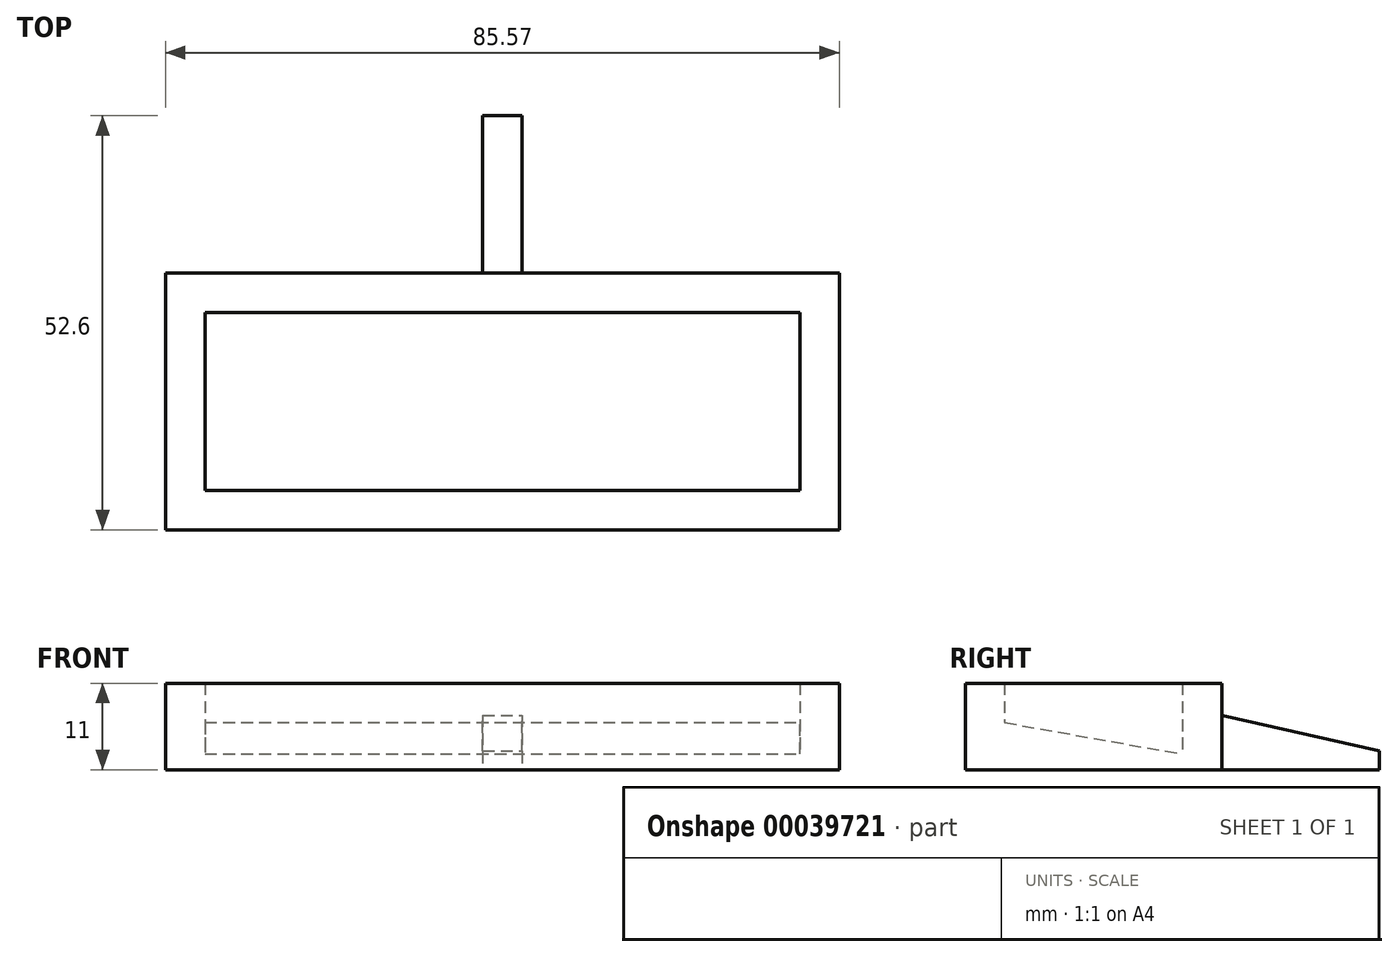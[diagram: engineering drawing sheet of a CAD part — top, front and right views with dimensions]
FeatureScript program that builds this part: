
annotation { "Feature Type Name" : "Feature", "Feature Type Description" : "" }
export const myFeature = defineFeature(function(context is Context, id is Id, definition is map)
    precondition{}
    {
        {
            var Q0;
            Q0=qCreatedBy(makeId("Top.planeOp"),FACE);
            var sketch = newSketch(context, id + "F0", { "sketchPlane" : qUnion([Q0])});
            skLineSegment(sketch, "E0.bottom", {"start": v(0, 0) * mm, "end": v(75.57, 0) * mm});
            skLineSegment(sketch, "E0.top", {"start": v(0, -22.6) * mm, "end": v(75.57, -22.6) * mm});
            skLineSegment(sketch, "E0.left", {"start": v(0, 0) * mm, "end": v(0, -22.6) * mm});
            skLineSegment(sketch, "E0.right", {"start": v(75.57, 0) * mm, "end": v(75.57, -22.6) * mm});
            skLineSegment(sketch, "E1.bottom", {"start": v(-5, 5) * mm, "end": v(80.57, 5) * mm});
            skLineSegment(sketch, "E1.top", {"start": v(-5, -27.6) * mm, "end": v(80.57, -27.6) * mm});
            skLineSegment(sketch, "E1.left", {"start": v(-5, 5) * mm, "end": v(-5, -27.6) * mm});
            skLineSegment(sketch, "E1.right", {"start": v(80.57, 5) * mm, "end": v(80.57, -27.6) * mm});
            skLineSegment(sketch, "E2.bottom", {"start": v(35.28, 25) * mm, "end": v(40.28, 25) * mm});
            skLineSegment(sketch, "E2.top", {"start": v(35.28, 5) * mm, "end": v(40.28, 5) * mm});
            skLineSegment(sketch, "E2.left", {"start": v(35.28, 25) * mm, "end": v(35.28, 5) * mm});
            skLineSegment(sketch, "E2.right", {"start": v(40.28, 25) * mm, "end": v(40.28, 5) * mm});
            skPoint(sketch, "E3", {"position": v(37.78, 5) * mm});
            skSolve(sketch);
        }
        {
            var Q0;
            Q0=makeQuery(id+"F0.imprint","IMPRINT",FACE,{"disambiguationData":[TD([[makeQuery(id+"F0.imprint","IMPRINT",EDGE,{"derivedFrom":sQuery(id+"F0.wireOp",EDGE,"E0.bottom")}),-1.0]])]});
            extrude(context, id + "F1", {"entities" : qUnion([Q0]), "depth" : 2 * mm});
        }
        {
            var Q0;
            Q0=makeQuery(id+"F0.imprint","IMPRINT",FACE,{"disambiguationData":[TD([[makeQuery(id+"F0.imprint","IMPRINT",EDGE,{"derivedFrom":sQuery(id+"F0.wireOp",EDGE,"E0.bottom")}),1.0]])]});
            var Q1;
            Q1=makeQuery(id+"F0.imprint","IMPRINT",FACE,{"disambiguationData":[TD([[makeQuery(id+"F0.imprint","IMPRINT",EDGE,{"derivedFrom":sQuery(id+"F0.wireOp",EDGE,"E2.bottom")}),-1.0]])]});
            extrude(context, id + "F2", {"entities" : qUnion([Q0, Q1]), "operationType" : NewBodyOperationType.ADD, "depth" : 11 * mm});
        }
        {
            var Q0;
            Q0=makeQuery(id+"F2.opExtrude","SWEPT_FACE",FACE,{"disambiguationData":[OSD([sQuery(id+"F0.wireOp",EDGE,"E0.right")])]});
            var sketch = newSketch(context, id + "F3", { "sketchPlane" : qUnion([Q0])});
            skLineSegment(sketch, "E4", {"start": v(0, 2) * mm, "end": v(22.6, 6) * mm});
            skSolve(sketch);
        }
        {
            var Q0;
            {var subQ2=sQuery(id+"F3.wireOp",EDGE,"E4");Q0=makeQuery(id+"F3.imprint","IMPRINT",FACE,{"disambiguationData":[TD([[makeQuery(id+"F3.imprint","IMPRINT",EDGE,{"derivedFrom":subQ2}),-1.0]])]});}
            extrude(context, id + "F4", {"entities" : qUnion([Q0]), "operationType" : NewBodyOperationType.ADD, "endBound" : BoundingType.UP_TO_NEXT, "depth" : 25 * mm});
        }
        {
            var Q0;
            Q0=makeQuery(id+"F2.opExtrude","SWEPT_FACE",FACE,{"disambiguationData":[OSD([sQuery(id+"F0.wireOp",EDGE,"E2.right")])]});
            var sketch = newSketch(context, id + "F5", { "sketchPlane" : qUnion([Q0])});
            skLineSegment(sketch, "E5", {"start": v(25, 2.39) * mm, "end": v(5, 6.94) * mm});
            skSolve(sketch);
        }
        {
            var Q0;
            {var subQ2=sQuery(id+"F5.wireOp",EDGE,"E5");Q0=makeQuery(id+"F5.imprint","IMPRINT",FACE,{"disambiguationData":[TD([[makeQuery(id+"F5.imprint","IMPRINT",EDGE,{"derivedFrom":subQ2}),-1.0]])]});}
            extrude(context, id + "F6", {"entities" : qUnion([Q0]), "operationType" : NewBodyOperationType.REMOVE, "oppositeDirection" : true, "depth" : 25 * mm});
        }
    });
